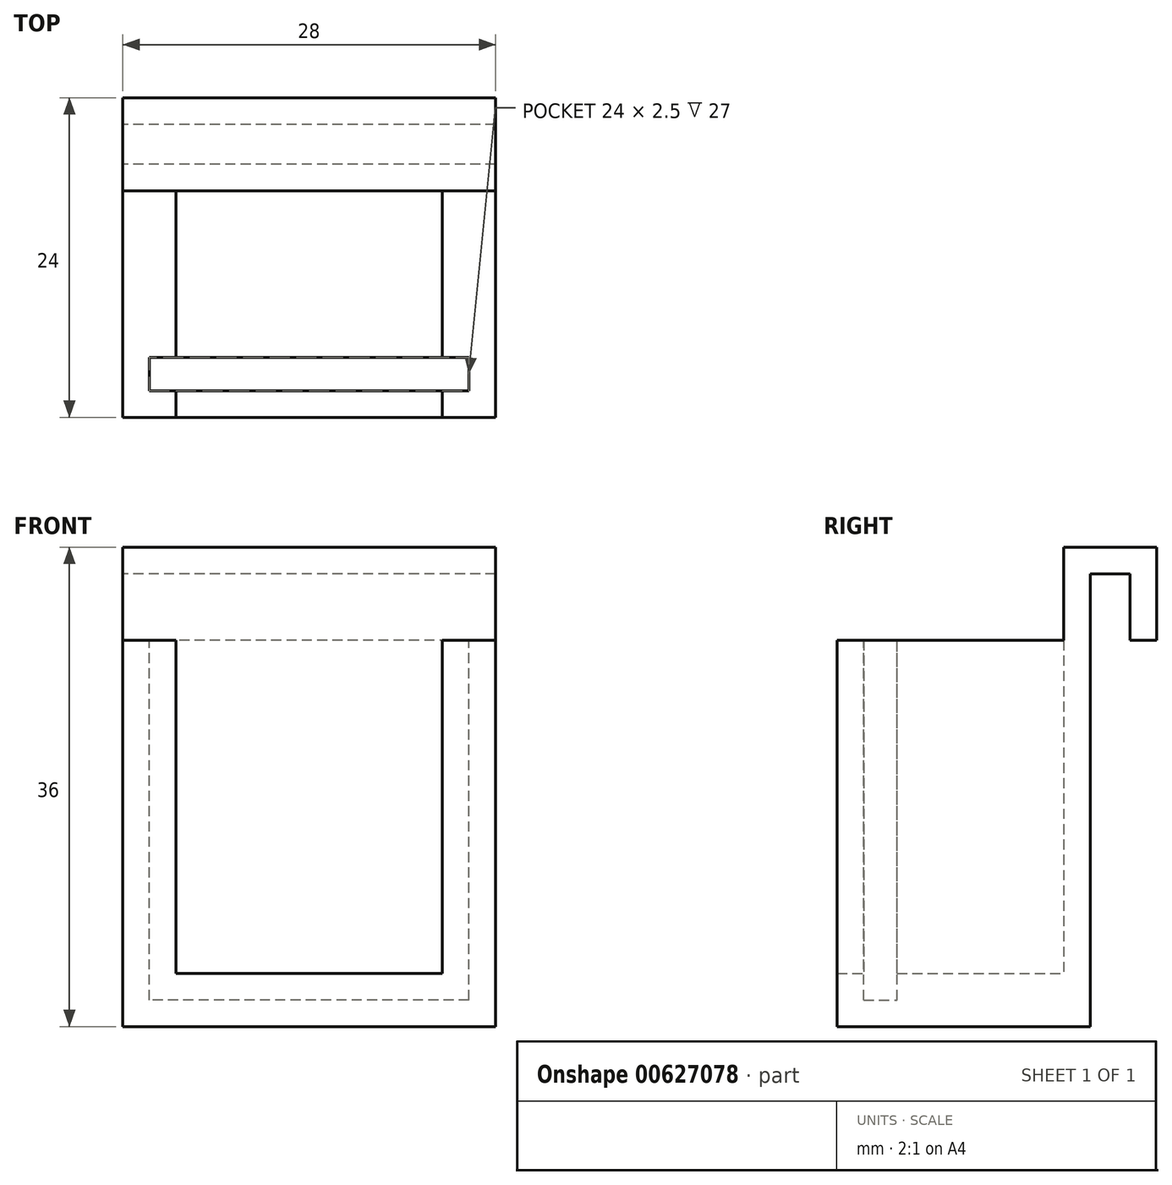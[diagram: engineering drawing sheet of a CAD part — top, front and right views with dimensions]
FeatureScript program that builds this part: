
annotation { "Feature Type Name" : "Feature", "Feature Type Description" : "" }
export const myFeature = defineFeature(function(context is Context, id is Id, definition is map)
    precondition{}
    {
        {
            var Q0;
            Q0=qCreatedBy(makeId("Top.planeOp"),FACE);
            var sketch = newSketch(context, id + "F0", { "sketchPlane" : qUnion([Q0])});
            skLineSegment(sketch, "E0.bottom", {"start": v(0, 0) * mm, "end": v(28, 0) * mm});
            skLineSegment(sketch, "E0.top", {"start": v(0, 19) * mm, "end": v(28, 19) * mm});
            skLineSegment(sketch, "E0.left", {"start": v(0, 0) * mm, "end": v(0, 19) * mm});
            skLineSegment(sketch, "E0.right", {"start": v(28, 0) * mm, "end": v(28, 19) * mm});
            skSolve(sketch);
        }
        {
            var Q0;
            Q0=makeQuery(id+"F0.imprint","IMPRINT",FACE,{"disambiguationData":[TD([[makeQuery(id+"F0.imprint","IMPRINT",EDGE,{"derivedFrom":sQuery(id+"F0.wireOp",EDGE,"E0.bottom")}),1.0]])]});
            extrude(context, id + "F1", {"entities" : qUnion([Q0]), "depth" : 4 * mm, "offsetDistance" : 25 * mm});
        }
        {
            var Q0;
            Q0=makeQuery(id+"F1.opExtrude","CAP_FACE",FACE,{"disambiguationData":[OSD([sQuery(id+"F0.wireOp",EDGE,"E0.bottom"),sQuery(id+"F0.wireOp",EDGE,"E0.top"),sQuery(id+"F0.wireOp",EDGE,"E0.left"),sQuery(id+"F0.wireOp",EDGE,"E0.right")])],"isStart":false});
            var sketch = newSketch(context, id + "F2", { "sketchPlane" : qUnion([Q0])});
            skLineSegment(sketch, "E1.bottom", {"start": v(0, 0) * mm, "end": v(4, 0) * mm});
            skLineSegment(sketch, "E1.top", {"start": v(0, 19) * mm, "end": v(4, 19) * mm});
            skLineSegment(sketch, "E1.left", {"start": v(0, 0) * mm, "end": v(0, 19) * mm});
            skLineSegment(sketch, "E1.right", {"start": v(4, 0) * mm, "end": v(4, 19) * mm});
            skLineSegment(sketch, "E2.bottom", {"start": v(28, 0) * mm, "end": v(24, 0) * mm});
            skLineSegment(sketch, "E2.top", {"start": v(28, 19) * mm, "end": v(24, 19) * mm});
            skLineSegment(sketch, "E2.left", {"start": v(28, 0) * mm, "end": v(28, 19) * mm});
            skLineSegment(sketch, "E2.right", {"start": v(24, 0) * mm, "end": v(24, 19) * mm});
            skLineSegment(sketch, "E3.bottom", {"start": v(4, 19) * mm, "end": v(24, 19) * mm});
            skLineSegment(sketch, "E3.top", {"start": v(4, 17) * mm, "end": v(24, 17) * mm});
            skLineSegment(sketch, "E3.left", {"start": v(4, 19) * mm, "end": v(4, 17) * mm});
            skLineSegment(sketch, "E3.right", {"start": v(24, 19) * mm, "end": v(24, 17) * mm});
            skSolve(sketch);
        }
        {
            var Q0;
            Q0 = qSketchRegion(id + "F2", true);
            extrude(context, id + "F3", {"entities" : qUnion([Q0]), "operationType" : NewBodyOperationType.ADD, "depth" : 25 * mm, "offsetDistance" : 25 * mm});
        }
        {
            var Q0;
            Q0=makeQuery(id+"F1.opExtrude","CAP_FACE",FACE,{"disambiguationData":[OSD([sQuery(id+"F0.wireOp",EDGE,"E0.bottom"),sQuery(id+"F0.wireOp",EDGE,"E0.top"),sQuery(id+"F0.wireOp",EDGE,"E0.left"),sQuery(id+"F0.wireOp",EDGE,"E0.right")])],"isStart":false});
            var sketch = newSketch(context, id + "F4", { "sketchPlane" : qUnion([Q0])});
            skLineSegment(sketch, "E4", {"start": v(4, 0) * mm, "end": v(4, 2) * mm, "construction": true});
            skLineSegment(sketch, "E5", {"start": v(4, 2) * mm, "end": v(2, 2) * mm, "construction": true});
            skLineSegment(sketch, "E6", {"start": v(24, 0) * mm, "end": v(24, 2) * mm, "construction": true});
            skLineSegment(sketch, "E7", {"start": v(24, 2) * mm, "end": v(26, 2) * mm, "construction": true});
            skLineSegment(sketch, "E8.bottom", {"start": v(26, 2) * mm, "end": v(2, 2) * mm});
            skLineSegment(sketch, "E8.top", {"start": v(26, 4.5) * mm, "end": v(2, 4.5) * mm});
            skLineSegment(sketch, "E8.left", {"start": v(26, 2) * mm, "end": v(26, 4.5) * mm});
            skLineSegment(sketch, "E8.right", {"start": v(2, 2) * mm, "end": v(2, 4.5) * mm});
            skSolve(sketch);
        }
        {
            var Q0;
            Q0 = qSketchRegion(id + "F4", true);
            extrude(context, id + "F5", {"entities" : qUnion([Q0]), "operationType" : NewBodyOperationType.REMOVE, "oppositeDirection" : true, "depth" : 2 * mm, "offsetDistance" : 25 * mm});
        }
        {
            var Q0;
            Q0=makeQuery(id+"F3.opExtrude","SWEPT_FACE",FACE,{"disambiguationData":[OSD([sQuery(id+"F2.wireOp",EDGE,"E2.right")])]});
            var sketch = newSketch(context, id + "F6", { "sketchPlane" : qUnion([Q0])});
            skLineSegment(sketch, "E9.0.0", {"start": v(-2, 4) * mm, "end": v(-4.5, 4) * mm});
            skLineSegment(sketch, "E9.0.1", {"start": v(-4.5, 4) * mm, "end": v(-4.5, 2) * mm});
            skLineSegment(sketch, "E9.0.2", {"start": v(-4.5, 2) * mm, "end": v(-2, 2) * mm});
            skLineSegment(sketch, "E9.0.3", {"start": v(-2, 2) * mm, "end": v(-2, 4) * mm});
            skLineSegment(sketch, "E10.bottom", {"start": v(-2, 2) * mm, "end": v(-4.5, 2) * mm});
            skLineSegment(sketch, "E10.top", {"start": v(-2, 29) * mm, "end": v(-4.5, 29) * mm});
            skLineSegment(sketch, "E10.left", {"start": v(-2, 2) * mm, "end": v(-2, 29) * mm});
            skLineSegment(sketch, "E10.right", {"start": v(-4.5, 2) * mm, "end": v(-4.5, 29) * mm});
            skSolve(sketch);
        }
        {
            var Q0;
            Q0 = qSketchRegion(id + "F6", true);
            extrude(context, id + "F7", {"entities" : qUnion([Q0]), "operationType" : NewBodyOperationType.REMOVE, "oppositeDirection" : true, "depth" : 2 * mm, "offsetDistance" : 25 * mm});
        }
        {
            var Q0;
            Q0=makeQuery(id+"F3.opExtrude","SWEPT_FACE",FACE,{"disambiguationData":[OSD([sQuery(id+"F2.wireOp",EDGE,"E1.right")])]});
            var sketch = newSketch(context, id + "F8", { "sketchPlane" : qUnion([Q0])});
            skLineSegment(sketch, "E11.0.0", {"start": v(4.5, 4) * mm, "end": v(2, 4) * mm});
            skLineSegment(sketch, "E11.0.1", {"start": v(2, 4) * mm, "end": v(2, 2) * mm});
            skLineSegment(sketch, "E11.0.2", {"start": v(2, 2) * mm, "end": v(4.5, 2) * mm});
            skLineSegment(sketch, "E11.0.3", {"start": v(4.5, 2) * mm, "end": v(4.5, 4) * mm});
            skLineSegment(sketch, "E12.bottom", {"start": v(4.5, 2) * mm, "end": v(2, 2) * mm});
            skLineSegment(sketch, "E12.top", {"start": v(4.5, 29) * mm, "end": v(2, 29) * mm});
            skLineSegment(sketch, "E12.left", {"start": v(4.5, 2) * mm, "end": v(4.5, 29) * mm});
            skLineSegment(sketch, "E12.right", {"start": v(2, 2) * mm, "end": v(2, 29) * mm});
            skSolve(sketch);
        }
        {
            var Q0;
            Q0 = qSketchRegion(id + "F8", true);
            extrude(context, id + "F9", {"entities" : qUnion([Q0]), "operationType" : NewBodyOperationType.REMOVE, "oppositeDirection" : true, "depth" : 2 * mm, "offsetDistance" : 25 * mm});
        }
        {
            var Q0;
            Q0=makeQuery(id+"F3.opExtrude","CAP_FACE",FACE,{"disambiguationData":[OSD([sQuery(id+"F2.wireOp",EDGE,"E1.bottom"),sQuery(id+"F2.wireOp",EDGE,"E1.top"),sQuery(id+"F2.wireOp",EDGE,"E1.left"),sQuery(id+"F2.wireOp",EDGE,"E1.right"),sQuery(id+"F2.wireOp",EDGE,"E2.bottom"),sQuery(id+"F2.wireOp",EDGE,"E2.top"),sQuery(id+"F2.wireOp",EDGE,"E2.left"),sQuery(id+"F2.wireOp",EDGE,"E2.right"),sQuery(id+"F2.wireOp",EDGE,"E3.bottom"),sQuery(id+"F2.wireOp",EDGE,"E3.top")])],"isStart":false});
            var sketch = newSketch(context, id + "F10", { "sketchPlane" : qUnion([Q0])});
            skLineSegment(sketch, "E13.bottom", {"start": v(28, 19) * mm, "end": v(0, 19) * mm});
            skLineSegment(sketch, "E13.top", {"start": v(28, 17) * mm, "end": v(0, 17) * mm});
            skLineSegment(sketch, "E13.left", {"start": v(28, 19) * mm, "end": v(28, 17) * mm});
            skLineSegment(sketch, "E13.right", {"start": v(0, 19) * mm, "end": v(0, 17) * mm});
            skSolve(sketch);
        }
        {
            var Q0;
            Q0 = qSketchRegion(id + "F10", true);
            extrude(context, id + "F11", {"entities" : qUnion([Q0]), "operationType" : NewBodyOperationType.ADD, "depth" : 7 * mm, "offsetDistance" : 25 * mm});
        }
        {
            var Q0;
            Q0=makeQuery(id+"F11.boolean.opBoolean","MERGE",FACE,{"derivedFrom":[makeQuery(id+"F3.boolean.opBoolean","MERGE",FACE,{"derivedFrom":[makeQuery(id+"F1.opExtrude","SWEPT_FACE",FACE,{"disambiguationData":[OSD([sQuery(id+"F0.wireOp",EDGE,"E0.top")])]}),makeQuery(id+"F3.opExtrude","SWEPT_FACE",FACE,{"disambiguationData":[OSD([sQuery(id+"F2.wireOp",EDGE,"E1.top"),sQuery(id+"F2.wireOp",EDGE,"E2.top"),sQuery(id+"F2.wireOp",EDGE,"E3.bottom")])]})]}),makeQuery(id+"F11.opExtrude","SWEPT_FACE",FACE,{"disambiguationData":[OSD([sQuery(id+"F10.wireOp",EDGE,"E13.bottom")])]})]});
            var sketch = newSketch(context, id + "F12", { "sketchPlane" : qUnion([Q0])});
            skLineSegment(sketch, "E14.bottom", {"start": v(-28, 36) * mm, "end": v(0, 36) * mm});
            skLineSegment(sketch, "E14.top", {"start": v(-28, 34) * mm, "end": v(0, 34) * mm});
            skLineSegment(sketch, "E14.left", {"start": v(-28, 36) * mm, "end": v(-28, 34) * mm});
            skLineSegment(sketch, "E14.right", {"start": v(0, 36) * mm, "end": v(0, 34) * mm});
            skSolve(sketch);
        }
        {
            var Q0;
            Q0 = qSketchRegion(id + "F12", true);
            extrude(context, id + "F13", {"entities" : qUnion([Q0]), "operationType" : NewBodyOperationType.ADD, "depth" : 5 * mm, "offsetDistance" : 25 * mm});
        }
        {
            var Q0;
            Q0=makeQuery(id+"F13.opExtrude","SWEPT_FACE",FACE,{"disambiguationData":[OSD([sQuery(id+"F12.wireOp",EDGE,"E14.top")])]});
            var sketch = newSketch(context, id + "F14", { "sketchPlane" : qUnion([Q0])});
            skLineSegment(sketch, "E15.bottom", {"start": v(28, -24) * mm, "end": v(0, -24) * mm});
            skLineSegment(sketch, "E15.top", {"start": v(28, -22) * mm, "end": v(0, -22) * mm});
            skLineSegment(sketch, "E15.left", {"start": v(28, -24) * mm, "end": v(28, -22) * mm});
            skLineSegment(sketch, "E15.right", {"start": v(0, -24) * mm, "end": v(0, -22) * mm});
            skSolve(sketch);
        }
        {
            var Q0;
            Q0 = qSketchRegion(id + "F14", true);
            extrude(context, id + "F15", {"entities" : qUnion([Q0]), "operationType" : NewBodyOperationType.ADD, "depth" : 5 * mm, "offsetDistance" : 25 * mm});
        }
    });
